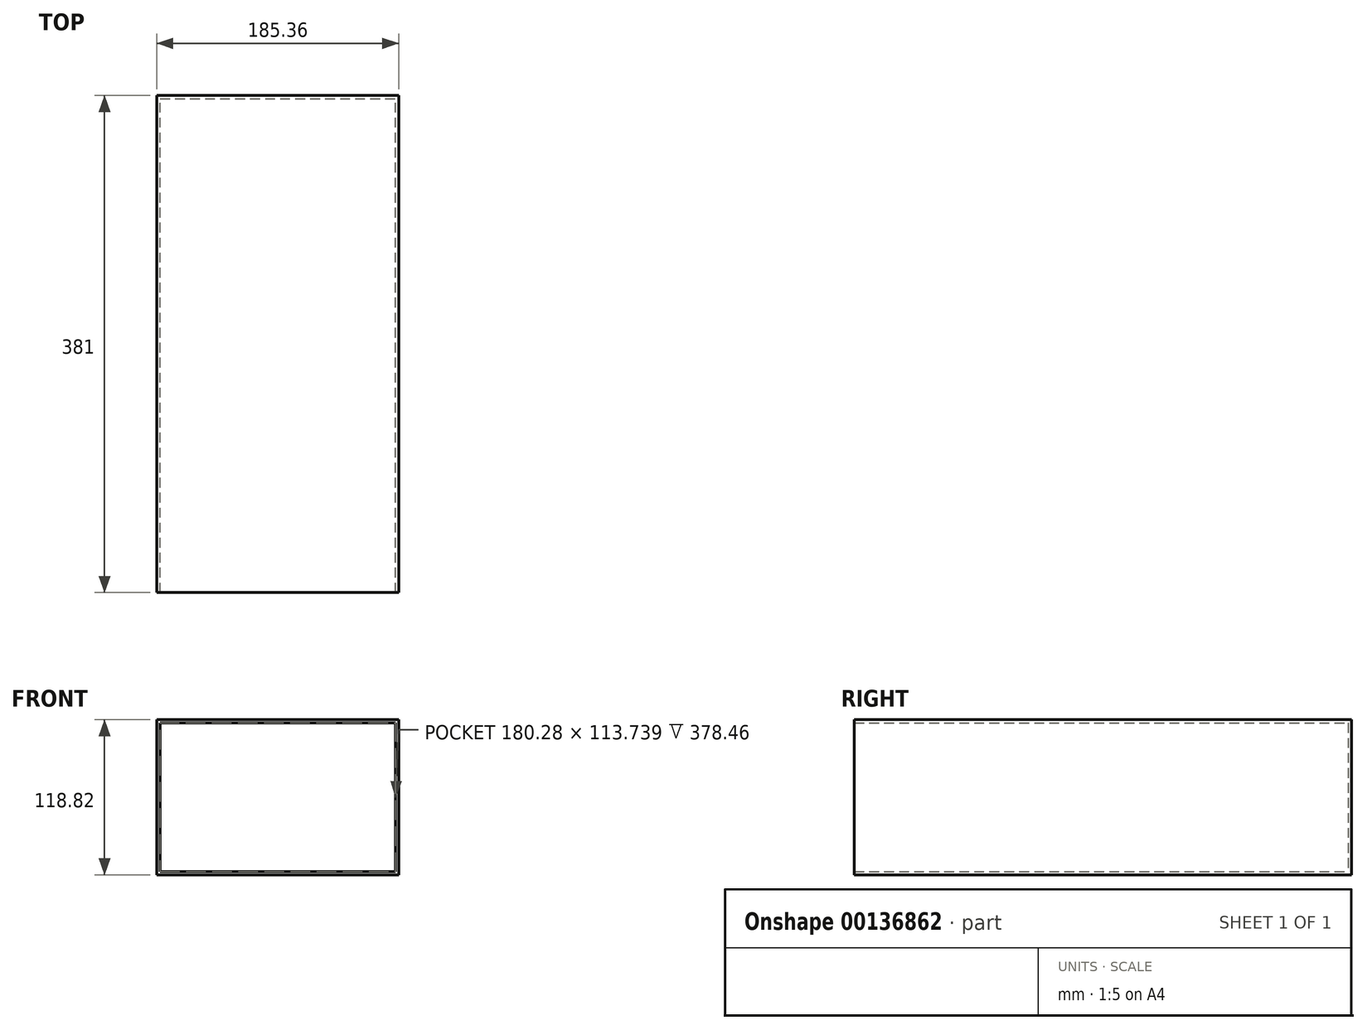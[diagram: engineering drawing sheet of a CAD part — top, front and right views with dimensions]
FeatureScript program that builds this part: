
annotation { "Feature Type Name" : "Feature", "Feature Type Description" : "" }
export const myFeature = defineFeature(function(context is Context, id is Id, definition is map)
    precondition{}
    {
        {
            var Q0;
            Q0=qCreatedBy(makeId("Front.planeOp"),FACE);
            var sketch = newSketch(context, id + "F0", { "sketchPlane" : qUnion([Q0])});
            skLineSegment(sketch, "E0.bottom", {"start": v(-84.52, 20.48) * mm, "end": v(100.84, 20.48) * mm});
            skLineSegment(sketch, "E0.top", {"start": v(-84.52, -98.34) * mm, "end": v(100.84, -98.34) * mm});
            skLineSegment(sketch, "E0.left", {"start": v(-84.52, 20.48) * mm, "end": v(-84.52, -98.34) * mm});
            skLineSegment(sketch, "E0.right", {"start": v(100.84, 20.48) * mm, "end": v(100.84, -98.34) * mm});
            skPoint(sketch, "E1", {"position": v(100.84, -38.93) * mm});
            skSolve(sketch);
        }
        {
            var Q0;
            Q0=makeQuery(id+"F0.imprint","IMPRINT",FACE,{"disambiguationData":[TD([[makeQuery(id+"F0.imprint","IMPRINT",EDGE,{"derivedFrom":sQuery(id+"F0.wireOp",EDGE,"E0.bottom")}),-1.0]])]});
            extrude(context, id + "F1", {"entities" : qUnion([Q0]), "endBound" : BoundingType.SYMMETRIC, "depth" : 381 * mm});
        }
        {
            var Q0;
            Q0=makeQuery(id+"F1.opExtrude","CAP_FACE",FACE,{"disambiguationData":[OSD([sQuery(id+"F0.wireOp",EDGE,"E0.bottom"),sQuery(id+"F0.wireOp",EDGE,"E0.top"),sQuery(id+"F0.wireOp",EDGE,"E0.left"),sQuery(id+"F0.wireOp",EDGE,"E0.right")])],"isStart":false});
            shell(context, id + "F2", {"entities" : qUnion([Q0]), "thickness" : 2.54 * mm});
        }
    });
